# Revit family: Domotics-DomesticRanges-GEWISS-SYSTEM_SIGNALLING-RINGER_2M
name_source: partatom
category: Apparecchi elettrici
revit_build: Autodesk Revit 2016 (Build: 20161004_0715(x64)
units: mm (PartAtom-declared; Revit-internal decimal feet)

## family parameters
Condiviso = Sì
Host = Superficie
Mantenere orientamento annotazione = Sì
Numero OmniClass = 23.80.50.11.14
Punto di calcolo locali = Sì
Quota connettore circolare = Usa diametro
Taglio con vuoti quando caricato = Sì
Tipo di parte = Normale
Titolo OmniClass = Switches

## types (4) — shared parameters
Carico apparente = 0 VA
Catalogue = DOMOTICS
Catalogue Range = SYSTEM - DOMESTIC RANGE
Description. = Ringer (3 inputs)
Electrocod = 0132
IDF = 621fbf66-cb59-43d8-ab59-d3c57e0493e2
IDT = 74ec7f65-ba21-4d7a-9308-5ca0a5175865
Immagine tipo = GW21643.jpg
Larghezza pulsante = 46 mm  [stored 0.150919 ft]
N. poli = 1
No. SYSTEM modules = 2
Power input = 3VA
Produttore = GEWISS S.p.A.
Prospetto di default = 1219 mm
SEO = Ringer
Simbolo = SIMBOLO SEGNAL ACUSTICA : SUONERIA E
Sound intensity = 75-90 dB (at 1 m)
Technical sheet = https://www.gewiss.com
Tipo = SYSTEM SEGNAL ACUSTICA EL_BASE : GW21643 - Nero - 230V
Type: = 3 shades
URL = https://www.gewiss.com
Version file RFA = 19.4
Volt = 230 V

## per-type parameters (varying)
| type | Colour | Descrizione | EAN code | Modello | Supply voltage | Voltage |
| GW20641 - Bell-3 input 12V 2M white | White | BELL-3 INPUT 12V 2M SY/WT | 8011564184862 | GW20641 | 12V ac/dc | 12V ac/dc |
| GW21641 - Bell-3 input 12V 2M black | Black | BELL-3 INPUT 12V 2M SY/BK | 8011564184855 | GW21641 | 12V ac/dc | 12V ac/dc |
| GW21643 - Bell-3 input 230V 2M black | Black | BELL-3 INPUT 230V 2M SY/BK | 8011564184879 | GW21643 | 230V ac - 50Hz | 230V ac - 50 Hz |
| GW20643 - Bell-3 input 230V 2M white | White | BELL-3 INPUT 230V 2M SY/WT | 8011564184886 | GW20643 | 230V ac - 50Hz | 230V ac - 50 Hz |

note: [stored X ft] marks values corroborated as IEEE doubles in the binary element streams (Revit-internal decimal feet)

## geometry (parser evidence)
native form markers: Sweep x2
no freeform markers — native parametric forms only
